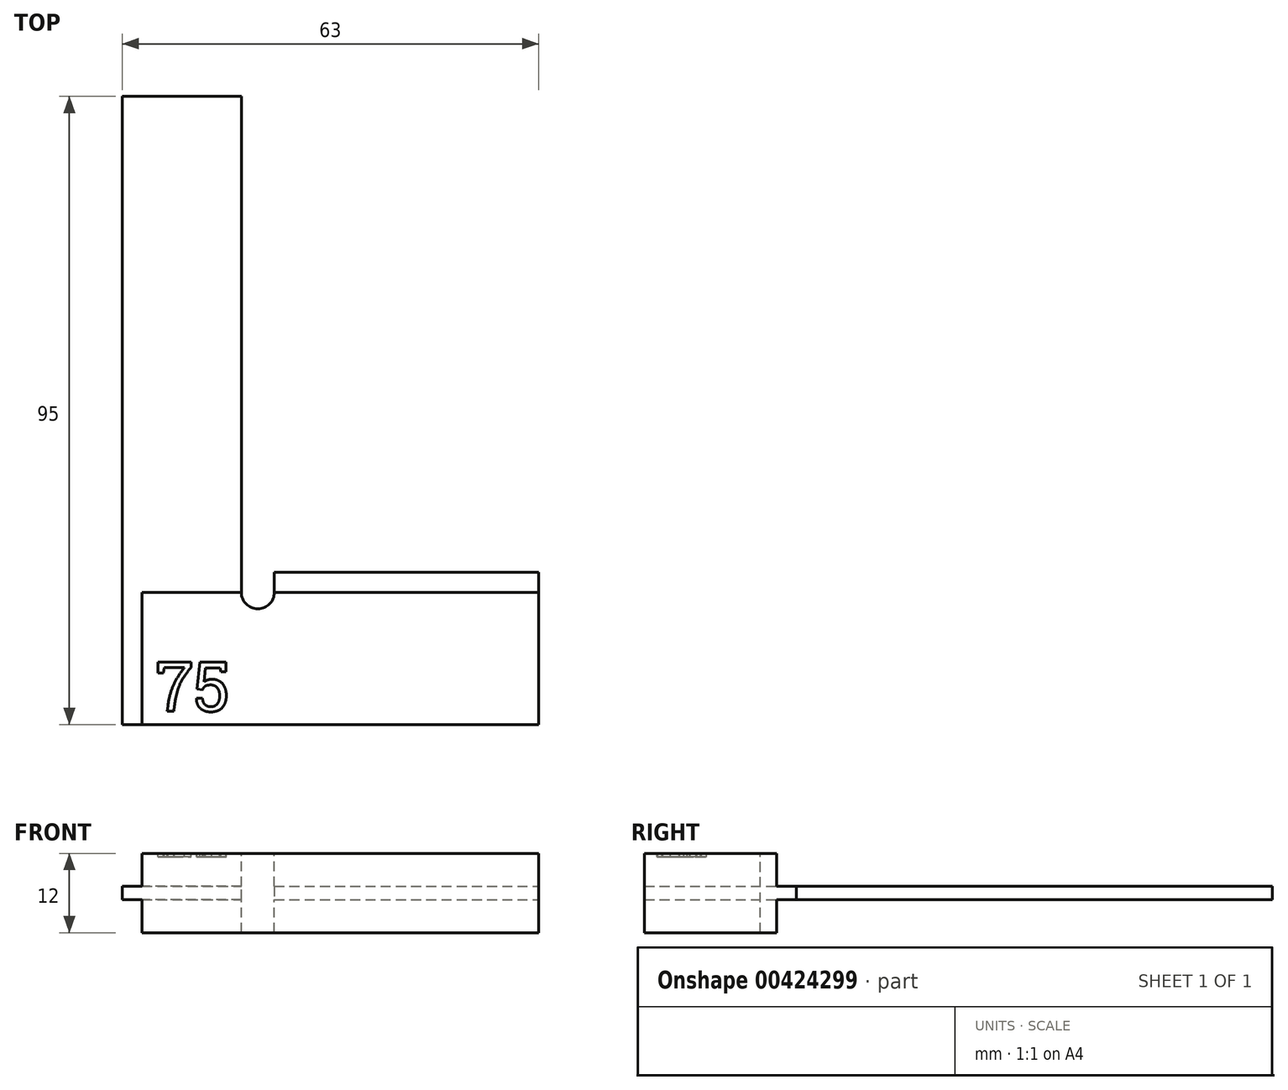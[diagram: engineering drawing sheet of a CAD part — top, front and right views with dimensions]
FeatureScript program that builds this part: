
annotation { "Feature Type Name" : "Feature", "Feature Type Description" : "" }
export const myFeature = defineFeature(function(context is Context, id is Id, definition is map)
    precondition{}
    {
        {
            var Q0;
            Q0=qCreatedBy(makeId("Top.planeOp"),FACE);
            var sketch = newSketch(context, id + "F0", { "sketchPlane" : qUnion([Q0])});
            skLineSegment(sketch, "E0.bottom", {"start": v(0, 0) * mm, "end": v(60, 0) * mm});
            skLineSegment(sketch, "E0.top", {"start": v(0, 20) * mm, "end": v(60, 20) * mm});
            skLineSegment(sketch, "E0.left", {"start": v(0, 0) * mm, "end": v(0, 20) * mm});
            skLineSegment(sketch, "E0.right", {"start": v(60, 0) * mm, "end": v(60, 20) * mm});
            skSolve(sketch);
        }
        {
            var Q0;
            Q0 = qSketchRegion(id + "F0", true);
            extrude(context, id + "F1", {"entities" : qUnion([Q0]), "depth" : 12 * mm});
        }
        {
            var Q0;
            Q0=makeQuery(id+"F1.opExtrude","SWEPT_FACE",FACE,{"disambiguationData":[OSD([sQuery(id+"F0.wireOp",EDGE,"E0.top")])]});
            var sketch = newSketch(context, id + "F2", { "sketchPlane" : qUnion([Q0])});
            skLineSegment(sketch, "E1", {"start": v(-60, 6) * mm, "end": v(0, 6) * mm, "construction": true});
            skPoint(sketch, "E2", {"position": v(-15, 6) * mm});
            skLineSegment(sketch, "E3.bottom", {"start": v(-15, 5) * mm, "end": v(-60, 5) * mm});
            skLineSegment(sketch, "E3.top", {"start": v(-15, 7) * mm, "end": v(-60, 7) * mm});
            skLineSegment(sketch, "E3.right", {"start": v(-60, 5) * mm, "end": v(-60, 7) * mm});
            skPoint(sketch, "E3.middle", {"position": v(-30, 6) * mm});
            skLineSegment(sketch, "E4", {"start": v(-15, 7) * mm, "end": v(-15, 5) * mm});
            skSolve(sketch);
        }
        {
            var Q0;
            Q0 = qSketchRegion(id + "F2", true);
            extrude(context, id + "F3", {"entities" : qUnion([Q0]), "operationType" : NewBodyOperationType.ADD, "depth" : 3 * mm});
        }
        {
            var Q0;
            Q0=makeQuery(id+"F1.opExtrude","SWEPT_FACE",FACE,{"disambiguationData":[OSD([sQuery(id+"F0.wireOp",EDGE,"E0.top")])]});
            var sketch = newSketch(context, id + "F4", { "sketchPlane" : qUnion([Q0])});
            skLineSegment(sketch, "E5", {"start": v(-15, 6) * mm, "end": v(0, 6) * mm, "construction": true});
            skLineSegment(sketch, "E6.bottom", {"start": v(-15, 5) * mm, "end": v(3, 5) * mm});
            skLineSegment(sketch, "E6.top", {"start": v(-15, 7) * mm, "end": v(3, 7) * mm});
            skLineSegment(sketch, "E6.left", {"start": v(-15, 5) * mm, "end": v(-15, 7) * mm});
            skPoint(sketch, "E6.middle", {"position": v(-6, 6) * mm});
            skLineSegment(sketch, "E7", {"start": v(3, 7) * mm, "end": v(3, 5) * mm});
            skSolve(sketch);
        }
        {
            var Q0;
            Q0 = qSketchRegion(id + "F4", true);
            var Q1;
            Q1=makeQuery(id+"F1.opExtrude","SWEPT_FACE",FACE,{"disambiguationData":[OSD([sQuery(id+"F0.wireOp",EDGE,"E0.bottom")])]});
            extrude(context, id + "F5", {"entities" : qUnion([Q0]), "operationType" : NewBodyOperationType.ADD, "depth" : 75 * mm, "hasSecondDirection" : true, "secondDirectionBound" : SecondDirectionBoundingType.UP_TO_SURFACE, "secondDirectionOppositeDirection" : true, "secondDirectionBoundEntityFace" : qUnion([Q1]), "secondDirectionDepth" : 25 * mm});
        }
        {
            var Q0;
            Q0=qCreatedBy(makeId("Top.planeOp"),FACE);
            var sketch = newSketch(context, id + "F6", { "sketchPlane" : qUnion([Q0])});
            skPoint(sketch, "E8.0", {"position": v(15, 20) * mm});
            skLineSegment(sketch, "E9.0", {"start": v(60, 20) * mm, "end": v(0, 20) * mm, "construction": true});
            skArc(sketch, "E10", {"start": v(15, 20) * mm, "mid": v(17.5, 17.5) * mm, "end": v(20, 20) * mm});
            skLineSegment(sketch, "E11", {"start": v(20, 20) * mm, "end": v(20, 25.7) * mm});
            skLineSegment(sketch, "E12", {"start": v(20, 25.7) * mm, "end": v(15, 25.7) * mm});
            skLineSegment(sketch, "E13", {"start": v(15, 25.7) * mm, "end": v(15, 20) * mm});
            skSolve(sketch);
        }
        {
            var Q0;
            Q0 = qSketchRegion(id + "F6", true);
            extrude(context, id + "F7", {"entities" : qUnion([Q0]), "operationType" : NewBodyOperationType.REMOVE, "endBound" : BoundingType.SYMMETRIC, "oppositeDirection" : true, "depth" : 25 * mm});
        }
        {
            var Q0;
            Q0=makeQuery(id+"F1.opExtrude","CAP_FACE",FACE,{"disambiguationData":[OSD([sQuery(id+"F0.wireOp",EDGE,"E0.bottom"),sQuery(id+"F0.wireOp",EDGE,"E0.top"),sQuery(id+"F0.wireOp",EDGE,"E0.left"),sQuery(id+"F0.wireOp",EDGE,"E0.right")])],"isStart":false});
            var sketch = newSketch(context, id + "F8", { "sketchPlane" : qUnion([Q0])});
            skText(sketch, "E14", { "text": "75", "fontName": "RobotoSlab-Regular.ttf"});
            const initialGuessF8  = {"E14": [0.002, 0.002, 1, 0, 0.0075]};
            skSetInitialGuess(sketch, initialGuessF8);
            skSolve(sketch);
        }
        {
            var Q0;
            Q0 = qSketchRegion(id + "F8", true);
            extrude(context, id + "F9", {"entities" : qUnion([Q0]), "operationType" : NewBodyOperationType.REMOVE, "oppositeDirection" : true, "depth" : 0.5 * mm});
        }
    });
